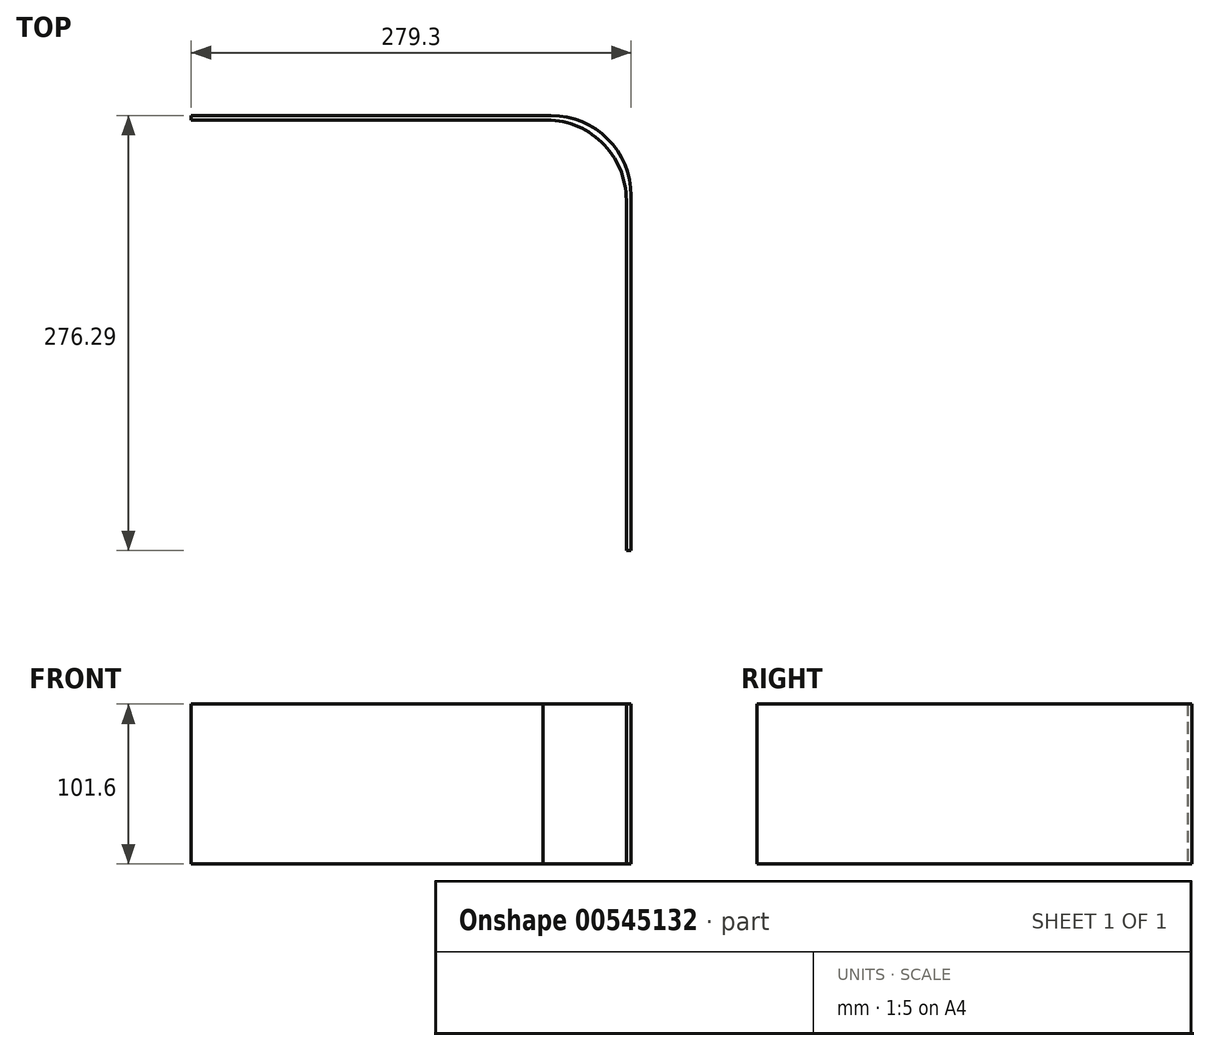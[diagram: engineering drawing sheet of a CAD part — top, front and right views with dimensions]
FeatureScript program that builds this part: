
annotation { "Feature Type Name" : "Feature", "Feature Type Description" : "" }
export const myFeature = defineFeature(function(context is Context, id is Id, definition is map)
    precondition{}
    {
        {
            var Q0;
            Q0=qCreatedBy(makeId("Top.planeOp"),FACE);
            var sketch = newSketch(context, id + "F0", { "sketchPlane" : qUnion([Q0])});
            skArc(sketch, "E0", {"start": v(50.8, 0) * mm, "mid": v(35.92, 35.92) * mm, "end": v(0, 50.8) * mm});
            skLineSegment(sketch, "E1", {"start": v(0, 50.8) * mm, "end": v(-76.1, 50.8) * mm});
            skLineSegment(sketch, "E2", {"start": v(50.8, 0) * mm, "end": v(50.8, -73.1) * mm});
            skArc(sketch, "E3", {"start": v(47.7, -2.86) * mm, "mid": v(32.07, 33.85) * mm, "end": v(-5.25, 47.94) * mm});
            skLineSegment(sketch, "E4", {"start": v(-5.25, 47.94) * mm, "end": v(-76.1, 47.94) * mm});
            skLineSegment(sketch, "E5", {"start": v(47.7, -2.86) * mm, "end": v(47.7, -73.1) * mm});
            skLineSegment(sketch, "E6", {"start": v(-76.1, 50.8) * mm, "end": v(-76.1, 47.94) * mm});
            skLineSegment(sketch, "E7", {"start": v(50.8, -73.1) * mm, "end": v(47.7, -73.1) * mm});
            skSolve(sketch);
        }
        {
            var Q0;
            Q0 = qSketchRegion(id + "F0", true);
            extrude(context, id + "F1", {"entities" : qUnion([Q0]), "depth" : 101.6 * mm, "offsetDistance" : 25.4 * mm});
        }
        {
            var Q0;
            Q0=makeQuery(id+"F1.opExtrude","SWEPT_FACE",FACE,{"disambiguationData":[OSD([sQuery(id+"F0.wireOp",EDGE,"E7")])]});
            extrude(context, id + "F2", {"entities" : qUnion([Q0]), "operationType" : NewBodyOperationType.ADD, "depth" : 152.4 * mm, "offsetDistance" : 25.4 * mm});
        }
        {
            var Q0;
            Q0=makeQuery(id+"F1.opExtrude","SWEPT_FACE",FACE,{"disambiguationData":[OSD([sQuery(id+"F0.wireOp",EDGE,"E6")])]});
            extrude(context, id + "F3", {"entities" : qUnion([Q0]), "operationType" : NewBodyOperationType.ADD, "depth" : 152.4 * mm, "offsetDistance" : 25.4 * mm});
        }
    });
